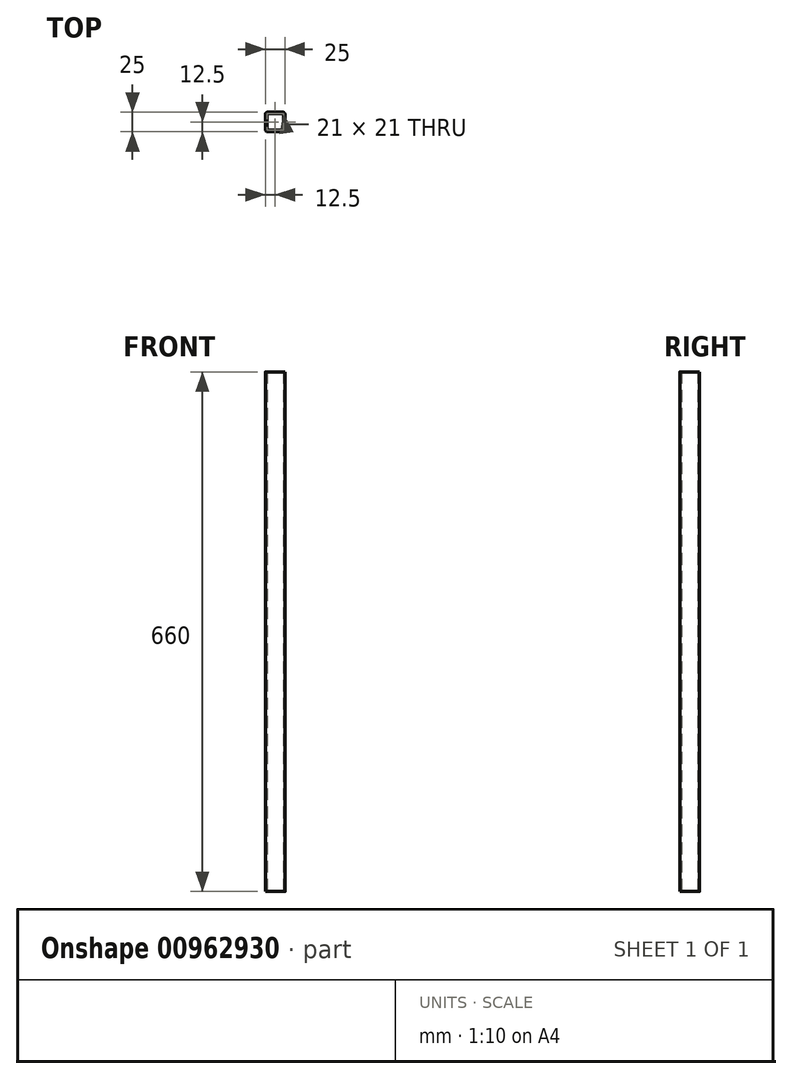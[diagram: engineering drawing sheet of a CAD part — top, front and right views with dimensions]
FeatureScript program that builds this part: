
annotation { "Feature Type Name" : "Feature", "Feature Type Description" : "" }
export const myFeature = defineFeature(function(context is Context, id is Id, definition is map)
    precondition{}
    {
        {
            var Q0;
            Q0=qCreatedBy(makeId("Top.planeOp"),FACE);
            var sketch = newSketch(context, id + "F0", { "sketchPlane" : qUnion([Q0])});
            skLineSegment(sketch, "E0.bottom", {"start": v(9.5, 12.5) * mm, "end": v(-9.5, 12.5) * mm});
            skLineSegment(sketch, "E0.top", {"start": v(9.5, -12.5) * mm, "end": v(-9.5, -12.5) * mm});
            skLineSegment(sketch, "E0.left", {"start": v(12.5, 9.5) * mm, "end": v(12.5, -9.5) * mm});
            skLineSegment(sketch, "E0.right", {"start": v(-12.5, 9.5) * mm, "end": v(-12.5, -9.5) * mm});
            skPoint(sketch, "E0.middle", {"position": v(0, 0) * mm});
            skPoint(sketch, "E1.visualSharp", {"position": v(-12.5, 12.5) * mm});
            skArc(sketch, "E1.filletArc", {"start": v(-9.5, 12.5) * mm, "mid": v(-11.62, 11.62) * mm, "end": v(-12.5, 9.5) * mm});
            skPoint(sketch, "E2.visualSharp", {"position": v(-12.5, -12.5) * mm});
            skArc(sketch, "E2.filletArc", {"start": v(-12.5, -9.5) * mm, "mid": v(-11.62, -11.62) * mm, "end": v(-9.5, -12.5) * mm});
            skPoint(sketch, "E3.visualSharp", {"position": v(12.5, -12.5) * mm});
            skArc(sketch, "E3.filletArc", {"start": v(9.5, -12.5) * mm, "mid": v(11.62, -11.62) * mm, "end": v(12.5, -9.5) * mm});
            skPoint(sketch, "E4.visualSharp", {"position": v(12.5, 12.5) * mm});
            skArc(sketch, "E4.filletArc", {"start": v(12.5, 9.5) * mm, "mid": v(11.62, 11.62) * mm, "end": v(9.5, 12.5) * mm});
            skLineSegment(sketch, "E5.0", {"start": v(10.5, 10.5) * mm, "end": v(-10.5, 10.5) * mm});
            skLineSegment(sketch, "E5.1", {"start": v(10.5, 10.5) * mm, "end": v(10.5, -10.5) * mm});
            skLineSegment(sketch, "E5.2", {"start": v(10.5, -10.5) * mm, "end": v(-10.5, -10.5) * mm});
            skLineSegment(sketch, "E5.3", {"start": v(-10.5, 10.5) * mm, "end": v(-10.5, -10.5) * mm});
            skSolve(sketch);
        }
        {
            var Q0;
            Q0=makeQuery(id+"F0.imprint","IMPRINT",FACE,{"disambiguationData":[TD([[makeQuery(id+"F0.imprint","IMPRINT",EDGE,{"derivedFrom":sQuery(id+"F0.wireOp",EDGE,"E0.bottom")}),1.0]])]});
            extrude(context, id + "F1", {"entities" : qUnion([Q0]), "depth" : 660 * mm, "offsetDistance" : 25 * mm});
        }
    });
